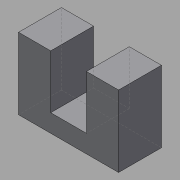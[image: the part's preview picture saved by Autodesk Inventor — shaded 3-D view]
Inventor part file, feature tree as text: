
AUTODESK INVENTOR PART (.ipt)
format: ipt  version: 2015 (Build 190159000, 159)  size: 77,824 bytes
history: native  units: in
note: dims shown in document units (in); Inventor stores cm internally (conversion verified against a paired STEP export)
features: other x3, sketch x2
ambient origin geometry x8: Origin, YZ Plane, XZ Plane, XY Plane, X Axis, Y Axis, Z Axis, Center Point
bodies: Solid1 (feature_tree)
feature tree (5):
  other  "opto_MIR3.ipt"
  other  "Solid1::opto_MIR3.ipt"
  other  "TaggingFeature1"
  sketch  "Sketch1"  dims[d0=0.3937in]
  sketch  "Sketch2"
